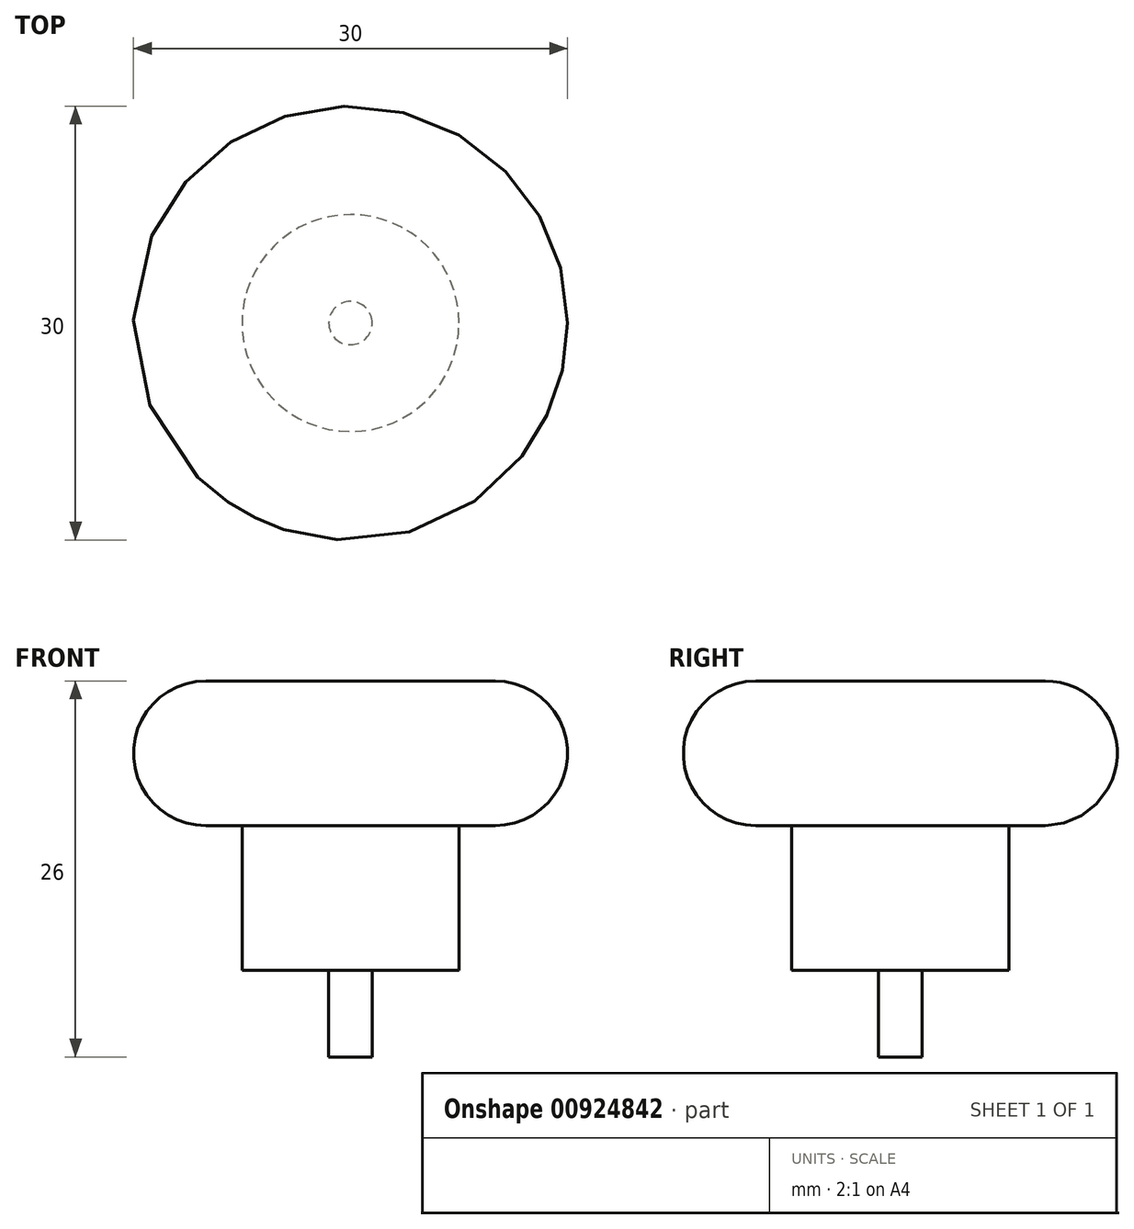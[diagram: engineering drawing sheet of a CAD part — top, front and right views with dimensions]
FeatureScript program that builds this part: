
annotation { "Feature Type Name" : "Feature", "Feature Type Description" : "" }
export const myFeature = defineFeature(function(context is Context, id is Id, definition is map)
    precondition{}
    {
        {
            var Q0;
            Q0=qCreatedBy(makeId("Top.planeOp"),FACE);
            var sketch = newSketch(context, id + "F0", { "sketchPlane" : qUnion([Q0])});
            skCircle(sketch, "E0", {"center": v(0, 0) * mm, "radius": 1.5 * mm});
            skCircle(sketch, "E1", {"center": v(0, 0) * mm, "radius": 7.5 * mm});
            skCircle(sketch, "E2.0", {"center": v(0, 0) * mm, "radius": 1 * mm});
            skSolve(sketch);
        }
        {
            var Q0;
            Q0=makeQuery(id+"F0.imprint","IMPRINT",FACE,{"disambiguationData":[TD([[makeQuery(id+"F0.imprint","IMPRINT",EDGE,{"derivedFrom":sQuery(id+"F0.wireOp",EDGE,"E0")}),-1.0]])]});
            var Q1;
            Q1=makeQuery(id+"F0.imprint","IMPRINT",FACE,{"disambiguationData":[TD([[makeQuery(id+"F0.imprint","IMPRINT",EDGE,{"derivedFrom":sQuery(id+"F0.wireOp",EDGE,"E0")}),1.0]])]});
            var Q2;
            Q2=makeQuery(id+"F0.imprint","IMPRINT",FACE,{"disambiguationData":[TD([[makeQuery(id+"F0.imprint","IMPRINT",EDGE,{"derivedFrom":sQuery(id+"F0.wireOp",EDGE,"E2.0")}),1.0]])]});
            extrude(context, id + "F1", {"entities" : qUnion([Q0, Q1, Q2]), "depth" : 10 * mm, "offsetDistance" : 25 * mm});
        }
        {
            var Q0;
            Q0=makeQuery(id+"F0.imprint","IMPRINT",FACE,{"disambiguationData":[TD([[makeQuery(id+"F0.imprint","IMPRINT",EDGE,{"derivedFrom":sQuery(id+"F0.wireOp",EDGE,"E0")}),1.0]])]});
            var Q1;
            Q1=makeQuery(id+"F0.imprint","IMPRINT",FACE,{"disambiguationData":[TD([[makeQuery(id+"F0.imprint","IMPRINT",EDGE,{"derivedFrom":sQuery(id+"F0.wireOp",EDGE,"E2.0")}),1.0]])]});
            extrude(context, id + "F2", {"entities" : qUnion([Q0, Q1]), "operationType" : NewBodyOperationType.ADD, "oppositeDirection" : true, "depth" : 6 * mm, "offsetDistance" : 25 * mm});
        }
        {
            var Q0;
            Q0=makeQuery(id+"F1.opExtrude","CAP_FACE",FACE,{"disambiguationData":[OSD([sQuery(id+"F0.wireOp",EDGE,"E1")])],"isStart":false});
            var sketch = newSketch(context, id + "F3", { "sketchPlane" : qUnion([Q0])});
            skCircle(sketch, "E3", {"center": v(0, 0) * mm, "radius": 15 * mm});
            skSolve(sketch);
        }
        {
            var Q0;
            Q0=makeQuery(id+"F3.imprint","IMPRINT",FACE,{"disambiguationData":[TD([[makeQuery(id+"F3.imprint","IMPRINT",EDGE,{"derivedFrom":sQuery(id+"F3.wireOp",EDGE,"E3")}),1.0]])]});
            var Q1;
            Q1=makeQuery(id+"F3.imprint","IMPRINT",FACE,{"disambiguationData":[TD([[makeQuery(id+"F3.imprint","IMPRINT",EDGE,{"derivedFrom":makeQuery(id+"F1.opExtrude","CAP_EDGE",EDGE,{"disambiguationData":[OSD([sQuery(id+"F0.wireOp",EDGE,"E1")])],"isStart":false})}),1.0]])]});
            extrude(context, id + "F4", {"entities" : qUnion([Q0, Q1]), "operationType" : NewBodyOperationType.ADD, "depth" : 10 * mm, "offsetDistance" : 25 * mm});
        }
        {
            var Q0;
            Q0=makeQuery(id+"F4.opExtrude","SWEPT_FACE",FACE,{"disambiguationData":[OSD([sQuery(id+"F3.wireOp",EDGE,"E3")])]});
            fillet(context, id + "F5", {"entities" : qUnion([Q0]), "radius" : 5 * mm, "tangentPropagation" : true, "allowEdgeOverflow" : false});
        }
    });
